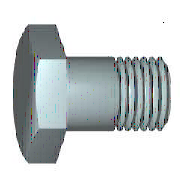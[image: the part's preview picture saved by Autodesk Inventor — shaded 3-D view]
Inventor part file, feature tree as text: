
AUTODESK INVENTOR PART (.ipt)
format: ipt  version: 2014 SP1 (Build 180222100, 222)  size: 185,856 bytes
history: native  units: mm (DEFAULTED — no unit token found)
features: sketch x2, extrude x1, chamfer x1, fillet x1, plane x1
ambient origin geometry x7: Origin, YZ Plane, XZ Plane, X Axis, Y Axis, Z Axis, Center Point
bodies: Solid1 (feature_tree), Body (feature_tree)
feature tree (6):
  extrude  "Head"  TaperAngle=90.0deg  [1 undecoded]
  chamfer  "Chamfer1"  [1 undecoded]
  fillet  "Fillet2"  [1 undecoded]
  plane  "Work Plane1"
  sketch  "Sketch1"  dims[d2=6.0mm d12=90.0deg]
  sketch  "Sketch2"  dims[d3=4.0mm d4=0.0mm d21=90.0deg d6=0.61345mm d7=0.61355mm d8=0.0mm d11=10.0mm d15=49.0mm d16=0.0mm d55=45.0deg d58=0.0mm d59=50.0mm d65=10.0mm d67=30.0deg d68=12.0mm d69=4.0mm d71=0.25mm d73=0.0mm]
note: 3 required parameter values undecoded (feature->parameter linkage not recoverable at this tier; creation-order binding heuristic only, values carry confidence <= 0.55)
